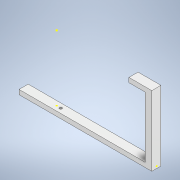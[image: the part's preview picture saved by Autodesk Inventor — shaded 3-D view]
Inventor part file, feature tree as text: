
AUTODESK INVENTOR PART (.ipt)
format: ipt  version: 2022 (Build 260153070, 153G)  size: 136,704 bytes
history: native  units: mm
features: sketch x8, extrude x4
ambient origin geometry x8: Origin, YZ Plane, XZ Plane, XY Plane, X Axis, Y Axis, Z Axis, Center Point
bodies: Solid1 (feature_tree)
feature tree (12):
  extrude  "Extrusion1"  Depth=14.0mm
  extrude  "Extrusion2"  Depth=152.4mm
  extrude  "Extrusion3"  TaperAngle=0.0deg  [1 undecoded]
  extrude  "Extrusion4"  Depth=14.0mm
  sketch  "Sketch10"  dims[d10=0.0mm]
  sketch  "Sketch11"  dims[d11=0.0mm]
  sketch  "Sketch12"  dims[d12=100.0mm d13=0.0mm]
  sketch  "Sketch13"  dims[d17=14.0mm d18=7.0mm d19=0.0mm d20=0.0mm d21=25.0mm d22=0.0mm d25=50.8mm d26=0.0mm d23=0.0mm d24=0.0mm d27=0.5mm d28=0.872665mm]
  sketch  "Sketch1"  dims[d0=7.0mm d1=14.0mm]
  sketch  "Sketch2"  dims[d2=152.4mm d3=0.0mm d4=4.0mm]
  sketch  "Sketch3"  dims[d5=6.0mm d6=0.0mm d7=0.0mm]
  sketch  "Sketch5"  dims[d8=10.0mm d9=14.0mm]
note: 1 required parameter value undecoded (feature->parameter linkage not recoverable at this tier; creation-order binding heuristic only, values carry confidence <= 0.55)
